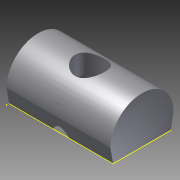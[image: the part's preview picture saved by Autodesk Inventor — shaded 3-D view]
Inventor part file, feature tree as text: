
AUTODESK INVENTOR PART (.ipt)
format: ipt  version: 2012 (Build 160160000, 160)  size: 126,976 bytes
history: native  units: mm
features: sketch x3, extrude x2, chamfer x2, hole x2
ambient origin geometry x8: Origin, YZ Plane, XZ Plane, XY Plane, X Axis, Y Axis, Z Axis, Center Point
bodies: Solid1 (feature_tree)
feature tree (9):
  extrude  "Extrusion1"  Depth=8.5mm
  extrude  "Extrusion2"  Depth=14.0mm TaperAngle=0.0deg
  chamfer  "Chamfer1"  Distance=2.0mm
  chamfer  "Chamfer2"  Distance=2.0mm
  sketch  "Sketch3"  dims[d12=3.9mm d13=7.0mm d14=4.0mm d15=6.0mm d16=4.0mm d17=2.0mm d18=90.0deg d19=8.0mm d20=20.594885mm d30=10.0mm d31=10.0mm d23=8.1mm d24=6.0mm d25=4.0mm d26=2.0mm d27=90.0deg d28=3.5mm d29=0.0mm]
  hole  "Hole1"  [1 undecoded]
  hole  "Hole2"  [1 undecoded]
  sketch  "Sketch1"  dims[d0=14.0mm d1=8.5mm]
  sketch  "Sketch2"  dims[d2=2.0mm d3=0.0mm d4=14.0mm d5=0.0mm d6=2.0mm d7=2.0mm d8=1.745329mm d9=2.0mm d10=2.0mm d11=1.745329mm]
note: 2 required parameter values undecoded (feature->parameter linkage not recoverable at this tier; creation-order binding heuristic only, values carry confidence <= 0.55)
